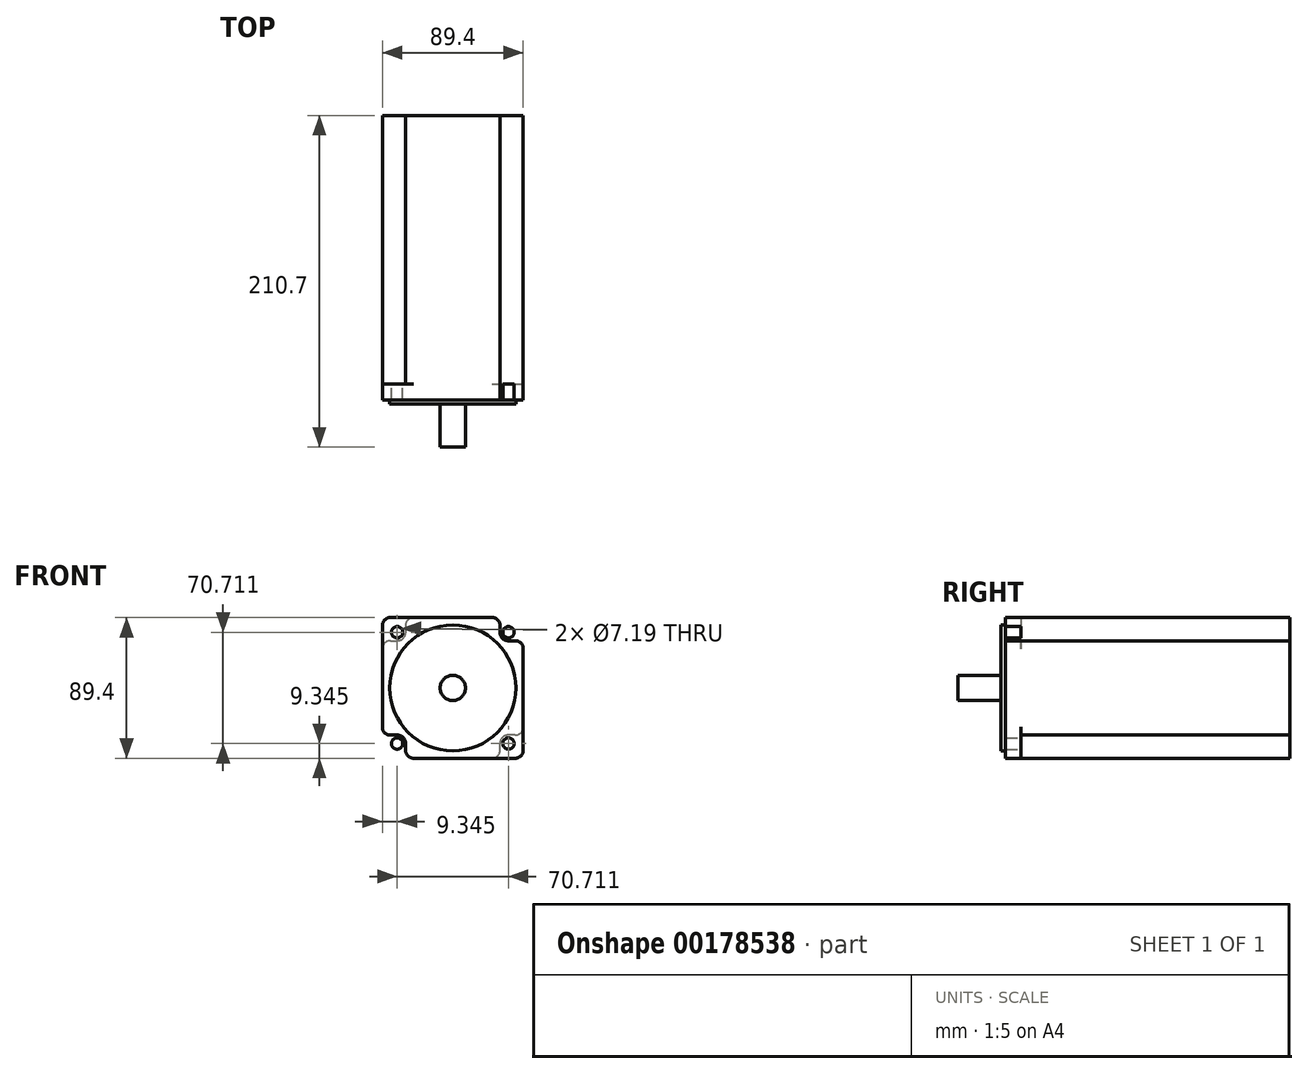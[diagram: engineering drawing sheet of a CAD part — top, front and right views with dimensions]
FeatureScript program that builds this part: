
annotation { "Feature Type Name" : "Feature", "Feature Type Description" : "" }
export const myFeature = defineFeature(function(context is Context, id is Id, definition is map)
    precondition{}
    {
        {
            var Q0;
            Q0=qCreatedBy(makeId("Front.planeOp"),FACE);
            var sketch = newSketch(context, id + "F0", { "sketchPlane" : qUnion([Q0])});
            skLineSegment(sketch, "E0.bottom", {"start": v(-44.7, -44.7) * mm, "end": v(44.7, -44.7) * mm});
            skLineSegment(sketch, "E0.top", {"start": v(-44.7, 44.7) * mm, "end": v(44.7, 44.7) * mm});
            skLineSegment(sketch, "E0.left", {"start": v(-44.7, -44.7) * mm, "end": v(-44.7, 44.7) * mm});
            skLineSegment(sketch, "E0.right", {"start": v(44.7, -44.7) * mm, "end": v(44.7, 44.7) * mm});
            skPoint(sketch, "E0.middle", {"position": v(0, 0) * mm});
            skCircle(sketch, "E1", {"center": v(0, 0) * mm, "radius": 40 * mm});
            skCircle(sketch, "E2", {"center": v(0, 0) * mm, "radius": 8 * mm});
            skCircle(sketch, "E3", {"center": v(-35.36, 35.36) * mm, "radius": 3.6 * mm});
            skCircle(sketch, "E4.MirrorC", {"center": v(35.36, 35.36) * mm, "radius": 3.6 * mm});
            skCircle(sketch, "E5.MirrorC", {"center": v(35.36, -35.36) * mm, "radius": 3.6 * mm});
            skCircle(sketch, "E6.MirrorC", {"center": v(-35.36, -35.36) * mm, "radius": 3.6 * mm});
            skLineSegment(sketch, "E7.bottom", {"start": v(-13.33, -44.7) * mm, "end": v(13.33, -44.7) * mm});
            skLineSegment(sketch, "E7.top", {"start": v(-13.34, -86.36) * mm, "end": v(13.34, -86.36) * mm});
            skLineSegment(sketch, "E7.left", {"start": v(-13.33, -44.7) * mm, "end": v(-13.34, -86.36) * mm});
            skLineSegment(sketch, "E7.right", {"start": v(13.34, -44.7) * mm, "end": v(13.33, -86.36) * mm});
            skCircle(sketch, "E8", {"center": v(0, -73.02) * mm, "radius": 13.34 * mm});
            skLineSegment(sketch, "E9.bottom", {"start": v(-44.7, -44.7) * mm, "end": v(-29.97, -44.7) * mm});
            skLineSegment(sketch, "E9.top", {"start": v(-44.7, -29.97) * mm, "end": v(-29.97, -29.97) * mm});
            skLineSegment(sketch, "E9.left", {"start": v(-44.7, -44.7) * mm, "end": v(-44.7, -29.97) * mm});
            skLineSegment(sketch, "E9.right", {"start": v(-29.97, -44.7) * mm, "end": v(-29.97, -29.97) * mm});
            skLineSegment(sketch, "E10.MirrorCS", {"start": v(29.97, -44.7) * mm, "end": v(29.97, -29.97) * mm});
            skLineSegment(sketch, "E11.MirrorCS", {"start": v(44.7, -29.97) * mm, "end": v(29.97, -29.97) * mm});
            skLineSegment(sketch, "E12.MirrorCS", {"start": v(44.7, 29.97) * mm, "end": v(29.97, 29.97) * mm});
            skLineSegment(sketch, "E13.MirrorCS", {"start": v(29.97, 44.7) * mm, "end": v(29.97, 29.97) * mm});
            skLineSegment(sketch, "E14.MirrorCS", {"start": v(-44.7, 29.97) * mm, "end": v(-29.97, 29.97) * mm});
            skLineSegment(sketch, "E15.MirrorCS", {"start": v(-29.97, 44.7) * mm, "end": v(-29.97, 29.97) * mm});
            skSolve(sketch);
        }
        {
            var Q0;
            Q0=makeQuery(id+"F0.imprint","IMPRINT",FACE,{"disambiguationData":[TD([[makeQuery(id+"F0.imprint","IMPRINT",EDGE,{"derivedFrom":sQuery(id+"F0.wireOp",EDGE,"E1")}),-1.0]])]});
            var Q1;
            Q1=makeQuery(id+"F0.imprint","IMPRINT",FACE,{"disambiguationData":[TD([[makeQuery(id+"F0.imprint","IMPRINT",EDGE,{"derivedFrom":sQuery(id+"F0.wireOp",EDGE,"E1")}),1.0]])]});
            var Q2;
            Q2=makeQuery(id+"F0.imprint","IMPRINT",FACE,{"disambiguationData":[TD([[makeQuery(id+"F0.imprint","IMPRINT",EDGE,{"derivedFrom":sQuery(id+"F0.wireOp",EDGE,"E2")}),1.0]])]});
            extrude(context, id + "F1", {"entities" : qUnion([Q0, Q1, Q2]), "oppositeDirection" : true, "depth" : 170.7 * mm});
        }
        {
            var Q0;
            Q0=makeQuery(id+"F0.imprint","IMPRINT",FACE,{"disambiguationData":[TD([[makeQuery(id+"F0.imprint","IMPRINT",EDGE,{"derivedFrom":sQuery(id+"F0.wireOp",EDGE,"E1")}),-1.0]])]});
            var Q1;
            Q1=makeQuery(id+"F0.imprint","IMPRINT",FACE,{"disambiguationData":[TD([[makeQuery(id+"F0.imprint","IMPRINT",EDGE,{"derivedFrom":sQuery(id+"F0.wireOp",EDGE,"E3")}),-1.0]])]});
            var Q2;
            Q2=makeQuery(id+"F0.imprint","IMPRINT",FACE,{"disambiguationData":[TD([[makeQuery(id+"F0.imprint","IMPRINT",EDGE,{"derivedFrom":sQuery(id+"F0.wireOp",EDGE,"E4.MirrorC")}),1.0]])]});
            var Q3;
            Q3=makeQuery(id+"F0.imprint","IMPRINT",FACE,{"disambiguationData":[TD([[makeQuery(id+"F0.imprint","IMPRINT",EDGE,{"derivedFrom":sQuery(id+"F0.wireOp",EDGE,"E5.MirrorC")}),-1.0]])]});
            var Q4;
            Q4=makeQuery(id+"F0.imprint","IMPRINT",FACE,{"disambiguationData":[TD([[makeQuery(id+"F0.imprint","IMPRINT",EDGE,{"derivedFrom":sQuery(id+"F0.wireOp",EDGE,"E6.MirrorC")}),1.0]])]});
            extrude(context, id + "F2", {"entities" : qUnion([Q0, Q1, Q2, Q3, Q4]), "operationType" : NewBodyOperationType.ADD, "depth" : 9.9 * mm});
        }
        {
            var Q0;
            Q0=makeQuery(id+"F0.imprint","IMPRINT",FACE,{"disambiguationData":[TD([[makeQuery(id+"F0.imprint","IMPRINT",EDGE,{"derivedFrom":sQuery(id+"F0.wireOp",EDGE,"E1")}),1.0]])]});
            extrude(context, id + "F3", {"entities" : qUnion([Q0]), "operationType" : NewBodyOperationType.ADD, "depth" : 12.65 * mm});
        }
        {
            var Q0;
            Q0=makeQuery(id+"F0.imprint","IMPRINT",FACE,{"disambiguationData":[TD([[makeQuery(id+"F0.imprint","IMPRINT",EDGE,{"derivedFrom":sQuery(id+"F0.wireOp",EDGE,"E2")}),1.0]])]});
            extrude(context, id + "F4", {"entities" : qUnion([Q0]), "operationType" : NewBodyOperationType.ADD, "depth" : 40 * mm});
        }
        {
            var Q0;
            Q0=makeQuery(id+"F1.opExtrude","SWEPT_EDGE",EDGE,{"disambiguationData":[OSD([sQuery(id+"F0.wireOp",EDGE,"E0.right"),sQuery(id+"F0.wireOp",EDGE,"E12.MirrorCS")])]});
            var Q1;
            Q1=makeQuery(id+"F1.opExtrude","SWEPT_EDGE",EDGE,{"disambiguationData":[OSD([sQuery(id+"F0.wireOp",EDGE,"E0.top"),sQuery(id+"F0.wireOp",EDGE,"E13.MirrorCS")])]});
            var Q2;
            Q2=makeQuery(id+"F1.opExtrude","SWEPT_EDGE",EDGE,{"disambiguationData":[OSD([sQuery(id+"F0.wireOp",EDGE,"E0.right"),sQuery(id+"F0.wireOp",EDGE,"E11.MirrorCS")])]});
            var Q3;
            Q3=makeQuery(id+"F1.opExtrude","SWEPT_EDGE",EDGE,{"disambiguationData":[OSD([sQuery(id+"F0.wireOp",EDGE,"E0.bottom"),sQuery(id+"F0.wireOp",EDGE,"E10.MirrorCS")])]});
            var Q4;
            Q4=makeQuery(id+"F1.opExtrude","SWEPT_EDGE",EDGE,{"disambiguationData":[OSD([sQuery(id+"F0.wireOp",EDGE,"E0.bottom"),sQuery(id+"F0.wireOp",EDGE,"E9.bottom"),sQuery(id+"F0.wireOp",EDGE,"E9.right")])]});
            var Q5;
            Q5=makeQuery(id+"F1.opExtrude","SWEPT_EDGE",EDGE,{"disambiguationData":[OSD([sQuery(id+"F0.wireOp",EDGE,"E0.left"),sQuery(id+"F0.wireOp",EDGE,"E9.top"),sQuery(id+"F0.wireOp",EDGE,"E9.left")])]});
            var Q6;
            Q6=makeQuery(id+"F1.opExtrude","SWEPT_EDGE",EDGE,{"disambiguationData":[OSD([sQuery(id+"F0.wireOp",EDGE,"E0.top"),sQuery(id+"F0.wireOp",EDGE,"E15.MirrorCS")])]});
            var Q7;
            Q7=makeQuery(id+"F1.opExtrude","SWEPT_EDGE",EDGE,{"disambiguationData":[OSD([sQuery(id+"F0.wireOp",EDGE,"E14.MirrorCS"),sQuery(id+"F0.wireOp",EDGE,"E15.MirrorCS")])]});
            var Q8;
            Q8=makeQuery(id+"F1.opExtrude","SWEPT_EDGE",EDGE,{"disambiguationData":[OSD([sQuery(id+"F0.wireOp",EDGE,"E0.left"),sQuery(id+"F0.wireOp",EDGE,"E14.MirrorCS")])]});
            var Q9;
            Q9=makeQuery(id+"F1.opExtrude","SWEPT_EDGE",EDGE,{"disambiguationData":[OSD([sQuery(id+"F0.wireOp",EDGE,"E9.top"),sQuery(id+"F0.wireOp",EDGE,"E9.right")])]});
            var Q10;
            Q10=makeQuery(id+"F1.opExtrude","SWEPT_EDGE",EDGE,{"disambiguationData":[OSD([sQuery(id+"F0.wireOp",EDGE,"E10.MirrorCS"),sQuery(id+"F0.wireOp",EDGE,"E11.MirrorCS")])]});
            var Q11;
            Q11=makeQuery(id+"F1.opExtrude","SWEPT_EDGE",EDGE,{"disambiguationData":[OSD([sQuery(id+"F0.wireOp",EDGE,"E12.MirrorCS"),sQuery(id+"F0.wireOp",EDGE,"E13.MirrorCS")])]});
            fillet(context, id + "F5", {"entities" : qUnion([Q0, Q1, Q2, Q3, Q4, Q5, Q6, Q7, Q8, Q9, Q10, Q11]), "radius" : 5.08 * mm, "tangentPropagation" : true, "allowEdgeOverflow" : false});
        }
        {
            var Q0;
            Q0=makeQuery(id+"F2.opExtrude","SWEPT_EDGE",EDGE,{"disambiguationData":[OSD([sQuery(id+"F0.wireOp",EDGE,"E0.top"),sQuery(id+"F0.wireOp",EDGE,"E0.left")])]});
            var Q1;
            Q1=makeQuery(id+"F2.opExtrude","SWEPT_EDGE",EDGE,{"disambiguationData":[OSD([sQuery(id+"F0.wireOp",EDGE,"E9.bottom"),sQuery(id+"F0.wireOp",EDGE,"E9.left")])]});
            var Q2;
            Q2=makeQuery(id+"F2.opExtrude","SWEPT_EDGE",EDGE,{"disambiguationData":[OSD([sQuery(id+"F0.wireOp",EDGE,"E0.top"),sQuery(id+"F0.wireOp",EDGE,"E0.right")])]});
            var Q3;
            Q3=makeQuery(id+"F2.opExtrude","SWEPT_EDGE",EDGE,{"disambiguationData":[OSD([sQuery(id+"F0.wireOp",EDGE,"E0.bottom"),sQuery(id+"F0.wireOp",EDGE,"E0.right")])]});
            fillet(context, id + "F6", {"entities" : qUnion([Q0, Q1, Q2, Q3]), "radius" : 5.08 * mm, "tangentPropagation" : true, "allowEdgeOverflow" : false});
        }
    });
